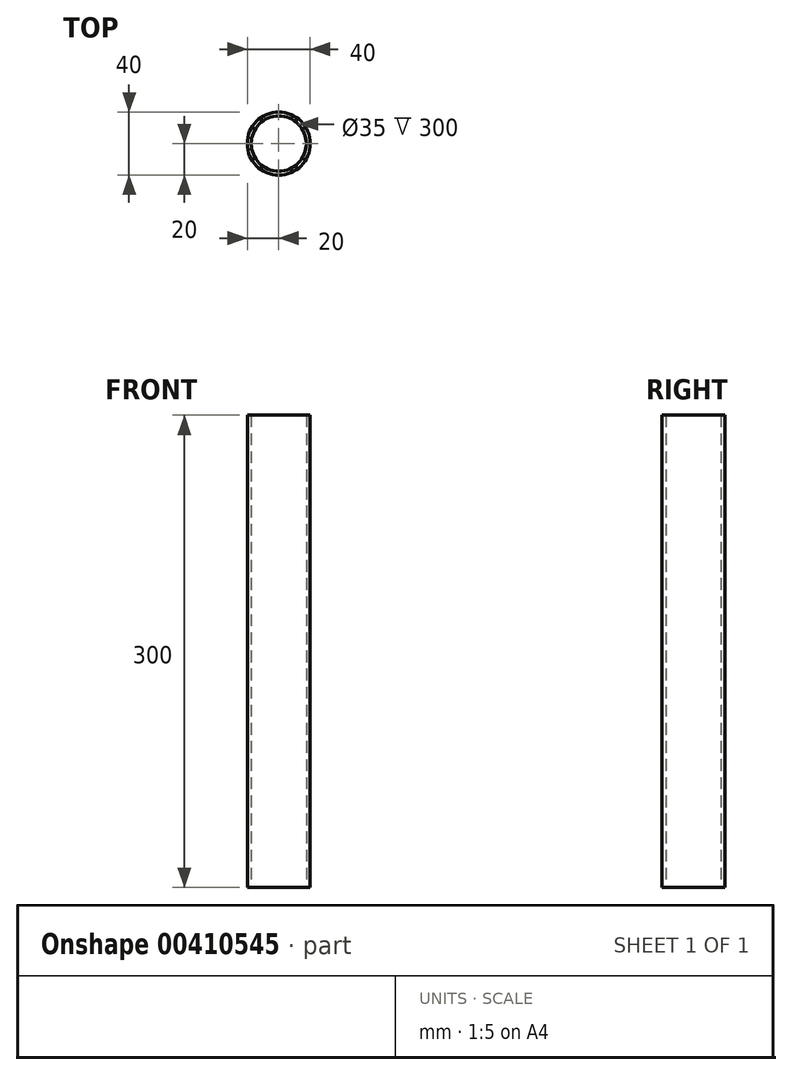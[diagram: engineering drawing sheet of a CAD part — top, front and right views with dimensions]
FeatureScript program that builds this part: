
annotation { "Feature Type Name" : "Feature", "Feature Type Description" : "" }
export const myFeature = defineFeature(function(context is Context, id is Id, definition is map)
    precondition{}
    {
        {
            var Q0;
            Q0=qCreatedBy(makeId("Top.planeOp"),FACE);
            var sketch = newSketch(context, id + "F0", { "sketchPlane" : qUnion([Q0])});
            skCircle(sketch, "E0", {"center": v(0, 0) * mm, "radius": 20 * mm});
            skCircle(sketch, "E1", {"center": v(0, 0) * mm, "radius": 17.5 * mm});
            skSolve(sketch);
        }
        {
            var Q0;
            Q0 = qSketchRegion(id + "F0", true);
            extrude(context, id + "F1", {"entities" : qUnion([Q0]), "depth" : 300 * mm});
        }
    });
